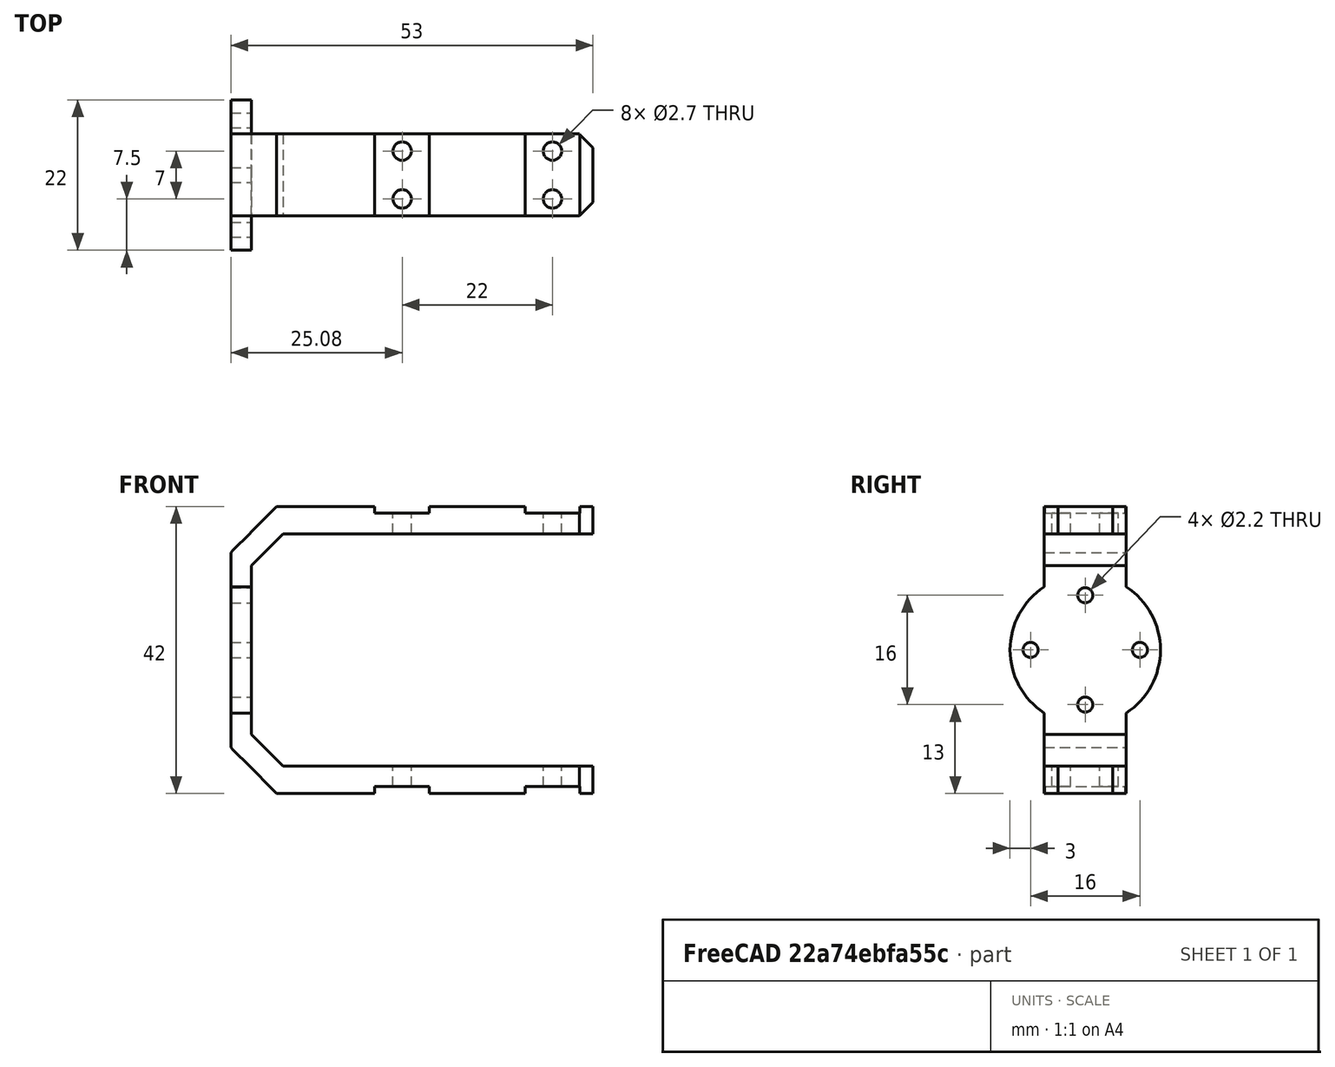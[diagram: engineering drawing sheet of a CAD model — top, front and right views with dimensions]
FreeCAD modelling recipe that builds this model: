
FCSTD DOCUMENT  (FreeCAD 0.15R4671 (Git))
Label: encoder_plate
License: All rights reserved
LicenseURL: http://en.wikipedia.org/wiki/All_rights_reserved
objects: Part::Cylinder×9, Part::Box×6, Part::MultiFuse×5, Part::Mirroring×4, Part::Cut×3, Part::Chamfer×1
note: 28 computed .brp shape members not serialized (recipe doc carries the construction recipe); baked Part::Feature solids carry a one-line shape summary decoded from their .brp

FEATURE [Part::Box] Box  label="Cube"
  Height = 4
  Length = 53
  Width = 12
FEATURE [Part::Mirroring] Part__Mirroring  label="Cube (Mirror #1)"
  Base = (0,0,-17)
  Normal = (0,0,1)
  Source = -> Box
FEATURE [Part::Box] Box001  label="Cube001"
  Height = 42
  Length = 3
  Placement = pos=(0,0,-38) rot=(0,0,1;0rad)
  Width = 12
FEATURE [Part::Cylinder] Cylinder
  Angle = 360
  Height = 3
  Placement = pos=(3,6,-17) rot=(0,-1,0;1.5708rad)
  Radius = 11
FEATURE [Part::Cylinder] Cylinder001
  Angle = 360
  Height = 100
  Placement = pos=(30.08,9.5,-50) rot=(0,0,1;0rad)
  Radius = 1.35
FEATURE [Part::Cylinder] Cylinder002
  Angle = 360
  Height = 100
  Placement = pos=(52.08,2.5,-50) rot=(0,0,1;0rad)
  Radius = 1.35
FEATURE [Part::Cylinder] Cylinder003
  Angle = 360
  Height = 100
  Placement = pos=(30.08,2.5,-50) rot=(0,0,1;0rad)
  Radius = 1.35
FEATURE [Part::Cylinder] Cylinder004
  Angle = 360
  Height = 100
  Placement = pos=(52.08,9.5,-50) rot=(0,0,1;0rad)
  Radius = 1.35
FEATURE [Part::Cylinder] Cylinder005
  Angle = 360
  Height = 10
  Placement = pos=(1,6,-9) rot=(0,1,0;1.5708rad)
  Radius = 1.1
FEATURE [Part::Cylinder] Cylinder006
  Angle = 360
  Height = 10
  Placement = pos=(1,6,-25) rot=(0,1,0;1.5708rad)
  Radius = 1.1
FEATURE [Part::Cylinder] Cylinder007
  Angle = 360
  Height = 10
  Placement = pos=(1,14,-17) rot=(0,1,0;1.5708rad)
  Radius = 1.1
FEATURE [Part::Cylinder] Cylinder008
  Angle = 360
  Height = 10
  Placement = pos=(1,-2,-17) rot=(0,1,0;1.5708rad)
  Radius = 1.1
FEATURE [Part::Box] Box002  label="Cube002"
  Height = 8
  Length = 4
  Placement = pos=(0,0,-2) rot=(0,1,0;0.785398rad)
  Width = 12
FEATURE [Part::Mirroring] Part__Mirroring001  label="Cube002 (Mirror #2)"
  Base = (0,0,-17)
  Normal = (0,0,1)
  Source = -> Box002
FEATURE [Part::MultiFuse] Fusion
  Shapes = -> [Box002,Part__Mirroring001,Part__Mirroring,Box,Box001,Cylinder]
FEATURE [Part::MultiFuse] Fusion001
  Placement = pos=(-5,0,0) rot=(0,0,1;0rad)
  Shapes = -> [Cylinder001,Cylinder003,Cylinder002,Cylinder006,Cylinder007,Cylinder008,Cylinder004,Cylinder005]
FEATURE [Part::Box] Box003  label="Cube003"
  Height = 12
  Length = 9
  Placement = pos=(-7,-1,3) rot=(0,1,0;0.785398rad)
  Width = 14
FEATURE [Part::Mirroring] Part__Mirroring002  label="Cube003 (Mirror #3)"
  Base = (0,0,-17)
  Normal = (0,0,1)
  Source = -> Box003
FEATURE [Part::MultiFuse] Fusion002
  Shapes = -> [Part__Mirroring002,Box003]
FEATURE [Part::Cut] Cut
  Base = -> Fusion
  Tool = -> Fusion002
FEATURE [Part::Cut] Cut001
  Base = -> Cut
  Tool = -> Fusion001
FEATURE [Part::Chamfer] Chamfer
  Base = -> Cut001
  Edges = 4 edges r=2: [Edge11,Edge17,Edge128,Edge138]
FEATURE [Part::Box] Box004  label="Cube004"
  Height = 1
  Length = 8
  Placement = pos=(26.08,0,3) rot=(0,0,1;0rad)
  Width = 12
FEATURE [Part::Box] Box005  label="Cube005"
  Height = 1
  Length = 8
  Placement = pos=(48.08,0,3) rot=(0,0,1;0rad)
  Width = 12
FEATURE [Part::MultiFuse] Fusion003
  Shapes = -> [Box004,Box005]
FEATURE [Part::Mirroring] Part__Mirroring003  label="Fusion003 (Mirror #4)"
  Base = (0,0,-17)
  Normal = (0,0,1)
  Source = -> Fusion003
FEATURE [Part::MultiFuse] Fusion004
  Placement = pos=(-5,0,0) rot=(0,0,1;0rad)
  Shapes = -> [Part__Mirroring003,Fusion003]
FEATURE [Part::Cut] Cut002
  Base = -> Chamfer
  Tool = -> Fusion004
